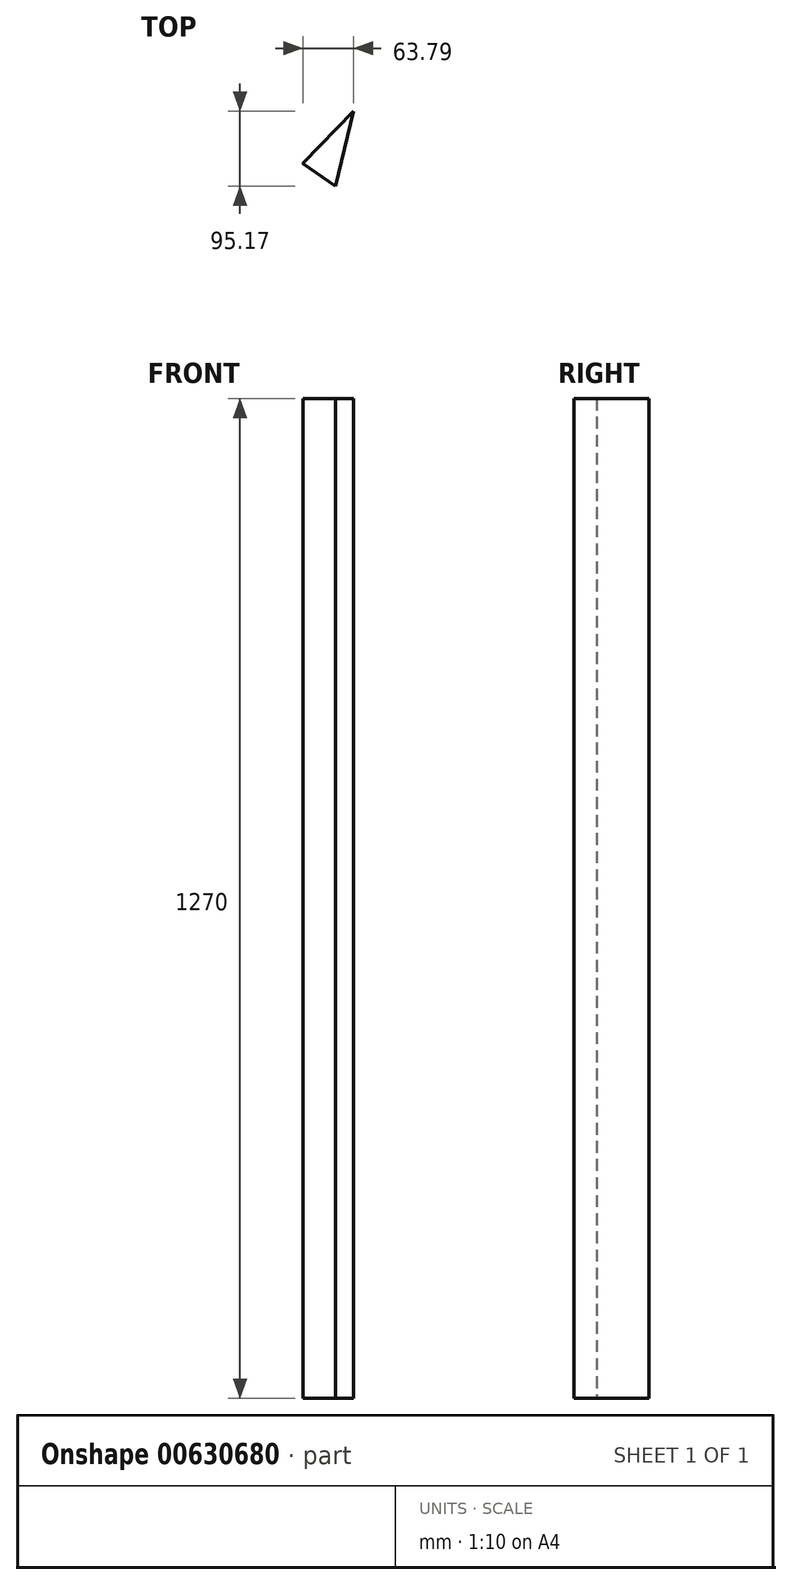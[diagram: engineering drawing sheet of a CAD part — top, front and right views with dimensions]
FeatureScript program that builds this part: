
annotation { "Feature Type Name" : "Feature", "Feature Type Description" : "" }
export const myFeature = defineFeature(function(context is Context, id is Id, definition is map)
    precondition{}
    {
        {
            var Q0;
            Q0=qCreatedBy(makeId("Top.planeOp"),FACE);
            var sketch = newSketch(context, id + "F0", { "sketchPlane" : qUnion([Q0])});
            skLineSegment(sketch, "E0", {"start": v(-0.56, -6.04) * mm, "end": v(63.06, 60.12) * mm});
            skLineSegment(sketch, "E1", {"start": v(63.06, 60.12) * mm, "end": v(40.14, -35.05) * mm});
            skLineSegment(sketch, "E2", {"start": v(40.14, -35.05) * mm, "end": v(-0.73, -6.78) * mm});
            skLineSegment(sketch, "E3", {"start": v(-0.73, -6.78) * mm, "end": v(-0.56, -6.04) * mm});
            skSolve(sketch);
        }
        {
            var Q0;
            Q0=makeQuery(id+"F0.imprint","IMPRINT",FACE,{"disambiguationData":[TD([[makeQuery(id+"F0.imprint","IMPRINT",EDGE,{"derivedFrom":sQuery(id+"F0.wireOp",EDGE,"E0")}),-1.0]])]});
            var Q1;
            Q1=sQuery(id+"F0.wireOp",EDGE,"E1");
            extrude(context, id + "F1", {"entities" : qUnion([Q0]), "surfaceEntities" : qUnion([Q1]), "depth" : 1270 * mm, "offsetDistance" : 25.4 * mm});
        }
    });
